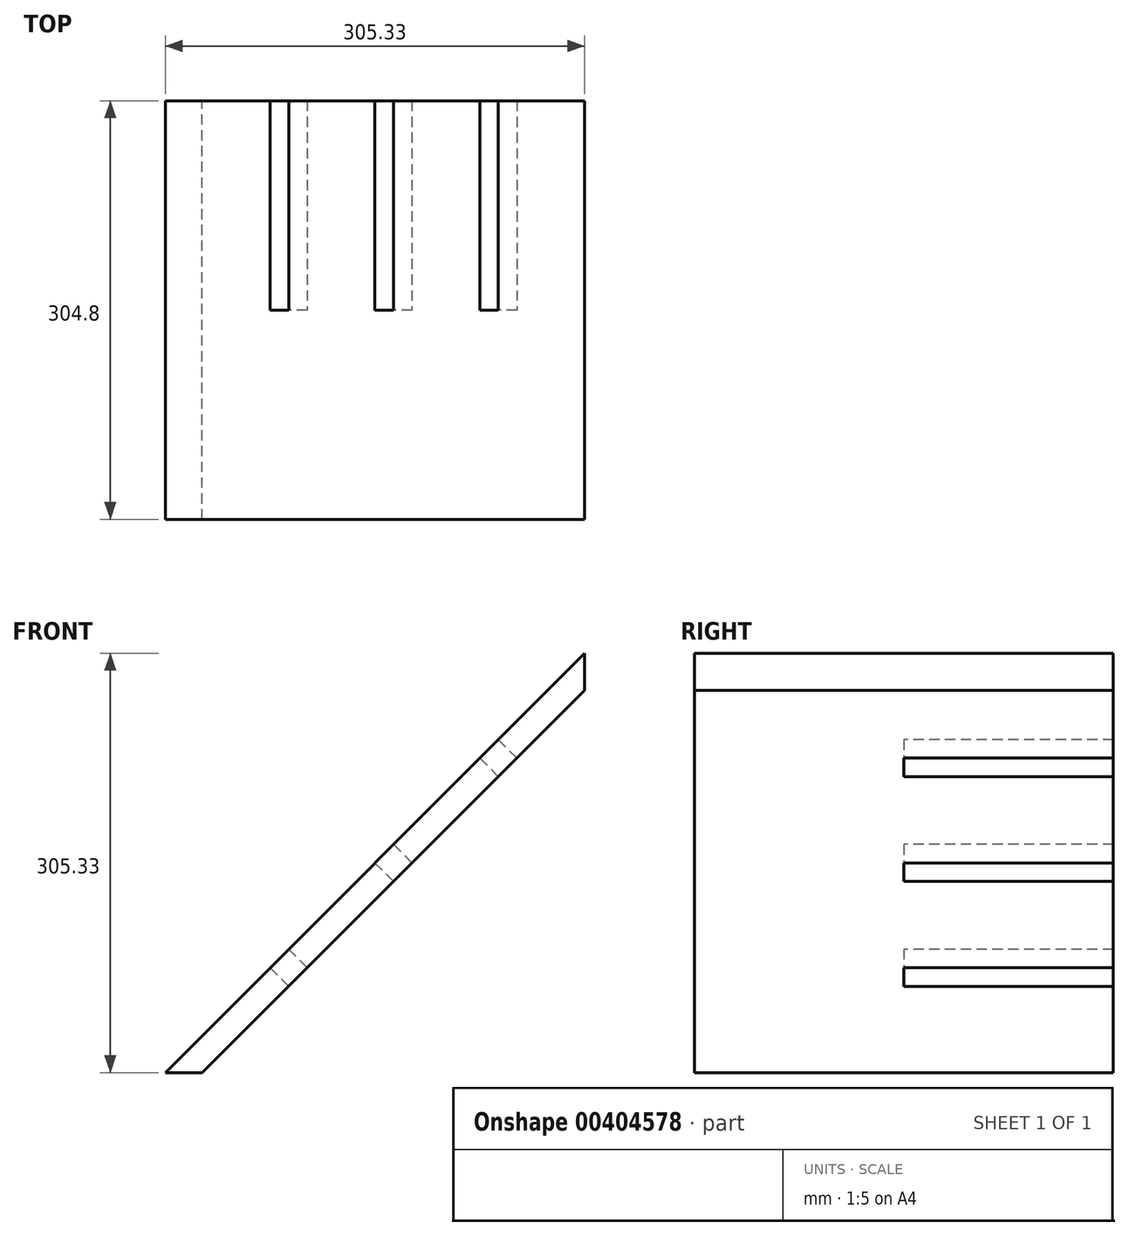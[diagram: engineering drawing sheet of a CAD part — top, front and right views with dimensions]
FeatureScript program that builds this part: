
annotation { "Feature Type Name" : "Feature", "Feature Type Description" : "" }
export const myFeature = defineFeature(function(context is Context, id is Id, definition is map)
    precondition{}
    {
        {
            var Q0;
            Q0=qCreatedBy(makeId("Front.planeOp"),FACE);
            var sketch = newSketch(context, id + "F0", { "sketchPlane" : qUnion([Q0])});
            skLineSegment(sketch, "E0", {"start": v(-337.22, 0) * mm, "end": v(-31.9, 305.33) * mm});
            skPoint(sketch, "E1.MirrorP", {"position": v(53.93, 355.6) * mm});
            skLineSegment(sketch, "E2.MirrorCS", {"start": v(-310.28, 0) * mm, "end": v(-31.9, 278.39) * mm});
            skLineSegment(sketch, "E3", {"start": v(-310.28, 0) * mm, "end": v(-337.22, 0) * mm});
            skLineSegment(sketch, "E4", {"start": v(-31.9, 305.33) * mm, "end": v(-31.9, 278.39) * mm});
            skSolve(sketch);
        }
        {
            var Q0;
            Q0=qSketchRegion(id+"F0",true);
            extrude(context, id + "F1", {"entities" : qUnion([Q0]), "endBound" : BoundingType.SYMMETRIC, "depth" : 304.8 * mm});
        }
        {
            var Q0;
            Q0=makeQuery(id+"F1.opExtrude","SWEPT_FACE",FACE,{"disambiguationData":[OSD([sQuery(id+"F0.wireOp",EDGE,"E2.MirrorCS")])]});
            var sketch = newSketch(context, id + "F2", { "sketchPlane" : qUnion([Q0])});
            skLineSegment(sketch, "E5.bottom", {"start": v(152.4, 104.45) * mm, "end": v(0, 104.45) * mm});
            skLineSegment(sketch, "E5.top", {"start": v(152.4, 85.4) * mm, "end": v(0, 85.4) * mm});
            skLineSegment(sketch, "E5.left", {"start": v(152.4, 104.45) * mm, "end": v(152.4, 85.4) * mm});
            skLineSegment(sketch, "E5.right", {"start": v(0, 104.45) * mm, "end": v(0, 85.4) * mm});
            skLineSegment(sketch, "E6.bottom", {"start": v(152.4, -3.5) * mm, "end": v(0, -3.5) * mm});
            skLineSegment(sketch, "E6.top", {"start": v(152.4, -22.55) * mm, "end": v(0, -22.55) * mm});
            skLineSegment(sketch, "E6.left", {"start": v(152.4, -3.5) * mm, "end": v(152.4, -22.55) * mm});
            skLineSegment(sketch, "E6.right", {"start": v(0, -3.5) * mm, "end": v(0, -22.55) * mm});
            skLineSegment(sketch, "E7.bottom", {"start": v(152.4, -111.45) * mm, "end": v(0, -111.45) * mm});
            skLineSegment(sketch, "E7.top", {"start": v(152.4, -130.5) * mm, "end": v(0, -130.5) * mm});
            skLineSegment(sketch, "E7.left", {"start": v(152.4, -111.45) * mm, "end": v(152.4, -130.5) * mm});
            skLineSegment(sketch, "E7.right", {"start": v(0, -111.45) * mm, "end": v(0, -130.5) * mm});
            skSolve(sketch);
        }
        {
            var Q0;
            Q0=qSketchRegion(id+"F2",true);
            extrude(context, id + "F3", {"entities" : qUnion([Q0]), "operationType" : NewBodyOperationType.REMOVE, "oppositeDirection" : true, "depth" : 19.05 * mm});
        }
    });
